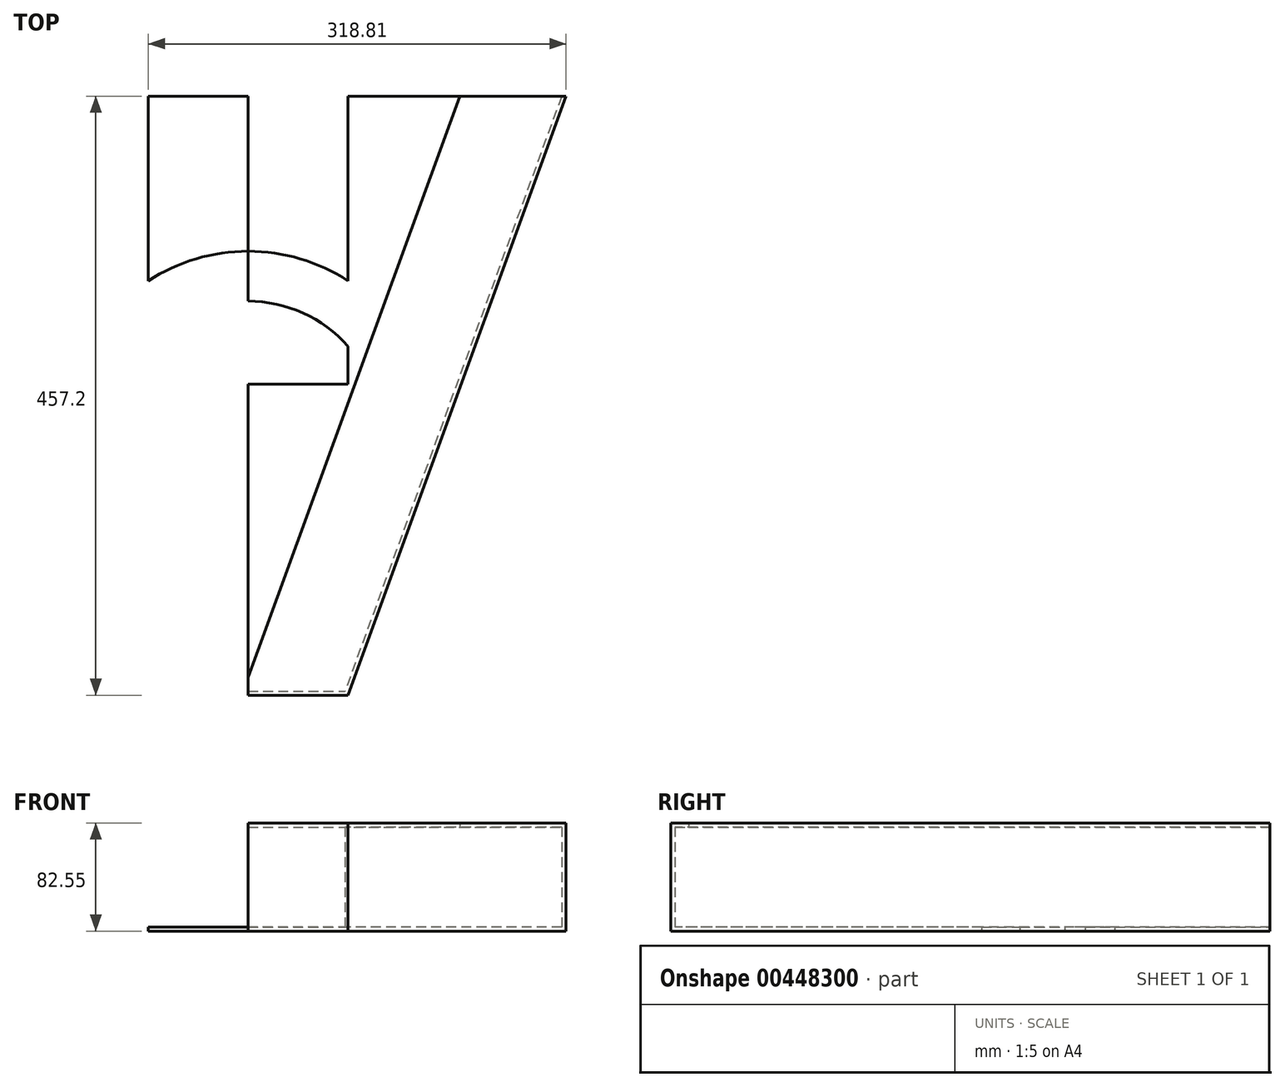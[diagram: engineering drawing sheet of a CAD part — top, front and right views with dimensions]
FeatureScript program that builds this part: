
annotation { "Feature Type Name" : "Feature", "Feature Type Description" : "" }
export const myFeature = defineFeature(function(context is Context, id is Id, definition is map)
    precondition{}
    {
        {
            var Q0;
            Q0=qCreatedBy(makeId("Top.planeOp"),FACE);
            var sketch = newSketch(context, id + "F0", { "sketchPlane" : qUnion([Q0])});
            skCircle(sketch, "E0", {"center": v(0, 0) * mm, "radius": 152.4 * mm});
            skLineSegment(sketch, "E1", {"start": v(-242.6, 220.97) * mm, "end": v(-76.2, -236.23) * mm});
            skLineSegment(sketch, "E2", {"start": v(-76.2, -236.23) * mm, "end": v(0, -236.23) * mm});
            skLineSegment(sketch, "E3", {"start": v(-242.6, 220.97) * mm, "end": v(0, 220.97) * mm});
            skLineSegment(sketch, "E4.MirrorCS", {"start": v(76.2, -236.23) * mm, "end": v(0, -236.23) * mm});
            skLineSegment(sketch, "E5.MirrorCS", {"start": v(242.6, 220.97) * mm, "end": v(0, 220.97) * mm});
            skLineSegment(sketch, "E6.MirrorCS", {"start": v(242.6, 220.97) * mm, "end": v(76.2, -236.23) * mm});
            skLineSegment(sketch, "E7", {"start": v(-76.2, -236.23) * mm, "end": v(-76.2, 220.97) * mm});
            skLineSegment(sketch, "E8.MirrorCS", {"start": v(76.2, -236.23) * mm, "end": v(76.2, 220.97) * mm});
            skLineSegment(sketch, "E9", {"start": v(-101.6, -166.44) * mm, "end": v(101.6, -166.44) * mm});
            skLineSegment(sketch, "E10", {"start": v(-242.6, 220.97) * mm, "end": v(-76.2, 145.12) * mm});
            skLineSegment(sketch, "E11.MirrorCS", {"start": v(242.6, 220.97) * mm, "end": v(76.2, 145.12) * mm});
            skLineSegment(sketch, "E12", {"start": v(-76.2, 145.12) * mm, "end": v(76.2, 145.12) * mm});
            skCircle(sketch, "E13", {"center": v(0, -37.13) * mm, "radius": 139.7 * mm});
            skLineSegment(sketch, "E14", {"start": v(-134.4, 0.97) * mm, "end": v(134.4, 0.97) * mm});
            skCircle(sketch, "E15", {"center": v(0, -37.13) * mm, "radius": 101.6 * mm});
            skLineSegment(sketch, "E16", {"start": v(0, 220.97) * mm, "end": v(0, -236.23) * mm});
            skSolve(sketch);
        }
        {
            var Q0;
            {var subQ0=sQuery(id+"F0.wireOp",EDGE,"E12");var subQ3=sQuery(id+"F0.wireOp",EDGE,"E0");var subQ4=makeQuery(id+"F0.imprint","INTERSECT",VERTEX,{"disambiguationData":[OD(0.0)],"derivedFrom":[subQ3,subQ0]});Q0=makeQuery(id+"F0.imprint","IMPRINT",FACE,{"disambiguationData":[TD([[makeQuery(id+"F0.imprint","IMPRINT",EDGE,{"disambiguationData":[TD([[subQ4,-1.0]])],"derivedFrom":subQ3}),-1.0]])]});}
            var Q1;
            {var subQ0=sQuery(id+"F0.wireOp",EDGE,"E12");var subQ1=sQuery(id+"F0.wireOp",EDGE,"E0");var subQ2=makeQuery(id+"F0.imprint","INTERSECT",VERTEX,{"disambiguationData":[OD(0.0)],"derivedFrom":[subQ1,subQ0]});Q1=makeQuery(id+"F0.imprint","IMPRINT",FACE,{"disambiguationData":[TD([[makeQuery(id+"F0.imprint","IMPRINT",EDGE,{"disambiguationData":[TD([[subQ2,-1.0]])],"derivedFrom":subQ1}),1.0]])]});}
            var Q2;
            {var subQ5=sQuery(id+"F0.wireOp",EDGE,"E12");var subQ6=sQuery(id+"F0.wireOp",EDGE,"E0");var subQ7=makeQuery(id+"F0.imprint","INTERSECT",VERTEX,{"disambiguationData":[OD(0.0)],"derivedFrom":[subQ6,subQ5]});Q2=makeQuery(id+"F0.imprint","IMPRINT",FACE,{"disambiguationData":[TD([[makeQuery(id+"F0.imprint","IMPRINT",EDGE,{"disambiguationData":[TD([[subQ7,1.0]])],"derivedFrom":subQ6}),1.0]])]});}
            var Q3;
            {var subQ0=sQuery(id+"F0.wireOp",EDGE,"E15");var subQ1=sQuery(id+"F0.wireOp",EDGE,"E8.MirrorCS");var subQ2=makeQuery(id+"F0.imprint","INTERSECT",VERTEX,{"disambiguationData":[OD(1.0)],"derivedFrom":[subQ1,subQ0]});Q3=makeQuery(id+"F0.imprint","IMPRINT",FACE,{"disambiguationData":[TD([[makeQuery(id+"F0.imprint","IMPRINT",EDGE,{"disambiguationData":[TD([[subQ2,-1.0]])],"derivedFrom":subQ1}),1.0]])]});}
            var Q4;
            {var subQ0=sQuery(id+"F0.wireOp",EDGE,"E15");var subQ1=sQuery(id+"F0.wireOp",EDGE,"E8.MirrorCS");var subQ2=makeQuery(id+"F0.imprint","INTERSECT",VERTEX,{"disambiguationData":[OD(1.0)],"derivedFrom":[subQ1,subQ0]});Q4=makeQuery(id+"F0.imprint","IMPRINT",FACE,{"disambiguationData":[TD([[makeQuery(id+"F0.imprint","IMPRINT",EDGE,{"disambiguationData":[TD([[subQ2,-1.0]])],"derivedFrom":subQ1}),-1.0]])]});}
            var Q5;
            {var subQ0=sQuery(id+"F0.wireOp",EDGE,"E14");var subQ1=sQuery(id+"F0.wireOp",EDGE,"E8.MirrorCS");var subQ2=makeQuery(id+"F0.imprint","INTERSECT",VERTEX,{"derivedFrom":[subQ1,subQ0]});Q5=makeQuery(id+"F0.imprint","IMPRINT",FACE,{"disambiguationData":[TD([[makeQuery(id+"F0.imprint","IMPRINT",EDGE,{"disambiguationData":[TD([[subQ2,-1.0]])],"derivedFrom":subQ1}),-1.0]])]});}
            var Q6;
            {var subQ0=sQuery(id+"F0.wireOp",EDGE,"E15");var subQ1=sQuery(id+"F0.wireOp",EDGE,"E8.MirrorCS");var subQ2=makeQuery(id+"F0.imprint","INTERSECT",VERTEX,{"disambiguationData":[OD(0.0)],"derivedFrom":[subQ1,subQ0]});Q6=makeQuery(id+"F0.imprint","IMPRINT",FACE,{"disambiguationData":[TD([[makeQuery(id+"F0.imprint","IMPRINT",EDGE,{"disambiguationData":[TD([[subQ2,-1.0]])],"derivedFrom":subQ1}),-1.0]])]});}
            var Q7;
            {var subQ0=sQuery(id+"F0.wireOp",EDGE,"E16");var subQ1=sQuery(id+"F0.wireOp",EDGE,"E0");var subQ2=makeQuery(id+"F0.imprint","INTERSECT",VERTEX,{"disambiguationData":[OD(1.0)],"derivedFrom":[subQ1,subQ0]});Q7=makeQuery(id+"F0.imprint","IMPRINT",FACE,{"disambiguationData":[TD([[makeQuery(id+"F0.imprint","IMPRINT",EDGE,{"disambiguationData":[TD([[subQ2,-1.0]])],"derivedFrom":subQ1}),1.0]])]});}
            var Q8;
            {var subQ0=sQuery(id+"F0.wireOp",EDGE,"E15");var subQ1=sQuery(id+"F0.wireOp",EDGE,"E8.MirrorCS");var subQ2=makeQuery(id+"F0.imprint","INTERSECT",VERTEX,{"disambiguationData":[OD(0.0)],"derivedFrom":[subQ1,subQ0]});Q8=makeQuery(id+"F0.imprint","IMPRINT",FACE,{"disambiguationData":[TD([[makeQuery(id+"F0.imprint","IMPRINT",EDGE,{"disambiguationData":[TD([[subQ2,-1.0]])],"derivedFrom":subQ1}),1.0]])]});}
            var Q9;
            {var subQ0=sQuery(id+"F0.wireOp",EDGE,"E16");var subQ6=sQuery(id+"F0.wireOp",EDGE,"E0");var subQ9=makeQuery(id+"F0.imprint","INTERSECT",VERTEX,{"disambiguationData":[OD(1.0)],"derivedFrom":[subQ6,subQ0]});Q9=makeQuery(id+"F0.imprint","IMPRINT",FACE,{"disambiguationData":[TD([[makeQuery(id+"F0.imprint","IMPRINT",EDGE,{"disambiguationData":[TD([[subQ9,-1.0]])],"derivedFrom":subQ6}),-1.0]])]});}
            var Q10;
            {var subQ7=sQuery(id+"F0.wireOp",EDGE,"E4.MirrorCS");Q10=makeQuery(id+"F0.imprint","IMPRINT",FACE,{"disambiguationData":[TD([[makeQuery(id+"F0.imprint","IMPRINT",EDGE,{"derivedFrom":subQ7}),-1.0]])]});}
            var Q11;
            {var subQ1=sQuery(id+"F0.wireOp",EDGE,"E6.MirrorCS");var subQ3=sQuery(id+"F0.wireOp",EDGE,"E9");var subQ4=makeQuery(id+"F0.imprint","INTERSECT",VERTEX,{"derivedFrom":[subQ1,subQ3]});Q11=makeQuery(id+"F0.imprint","IMPRINT",FACE,{"disambiguationData":[TD([[makeQuery(id+"F0.imprint","IMPRINT",EDGE,{"disambiguationData":[TD([[subQ4,1.0]])],"derivedFrom":subQ3}),-1.0]])]});}
            var Q12;
            {var subQ0=sQuery(id+"F0.wireOp",EDGE,"E9");var subQ1=sQuery(id+"F0.wireOp",EDGE,"E8.MirrorCS");var subQ2=makeQuery(id+"F0.imprint","INTERSECT",VERTEX,{"derivedFrom":[subQ1,subQ0]});Q12=makeQuery(id+"F0.imprint","IMPRINT",FACE,{"disambiguationData":[TD([[makeQuery(id+"F0.imprint","IMPRINT",EDGE,{"disambiguationData":[TD([[subQ2,-1.0]])],"derivedFrom":subQ1}),1.0]])]});}
            var Q13;
            {var subQ0=sQuery(id+"F0.wireOp",EDGE,"E16");var subQ1=sQuery(id+"F0.wireOp",EDGE,"E9");var subQ2=makeQuery(id+"F0.imprint","INTERSECT",VERTEX,{"derivedFrom":[subQ1,subQ0]});Q13=makeQuery(id+"F0.imprint","IMPRINT",FACE,{"disambiguationData":[TD([[makeQuery(id+"F0.imprint","IMPRINT",EDGE,{"disambiguationData":[TD([[subQ2,-1.0]])],"derivedFrom":subQ1}),-1.0]])]});}
            var Q14;
            {var subQ0=sQuery(id+"F0.wireOp",EDGE,"E9");var subQ1=sQuery(id+"F0.wireOp",EDGE,"E6.MirrorCS");var subQ2=makeQuery(id+"F0.imprint","INTERSECT",VERTEX,{"derivedFrom":[subQ1,subQ0]});Q14=makeQuery(id+"F0.imprint","IMPRINT",FACE,{"disambiguationData":[TD([[makeQuery(id+"F0.imprint","IMPRINT",EDGE,{"disambiguationData":[TD([[subQ2,1.0]])],"derivedFrom":subQ1}),-1.0]])]});}
            var Q15;
            {var subQ0=sQuery(id+"F0.wireOp",EDGE,"E8.MirrorCS");var subQ1=sQuery(id+"F0.wireOp",EDGE,"E0");var subQ2=makeQuery(id+"F0.imprint","INTERSECT",VERTEX,{"disambiguationData":[OD(1.0)],"derivedFrom":[subQ1,subQ0]});Q15=makeQuery(id+"F0.imprint","IMPRINT",FACE,{"disambiguationData":[TD([[makeQuery(id+"F0.imprint","IMPRINT",EDGE,{"disambiguationData":[TD([[subQ2,-1.0]])],"derivedFrom":subQ1}),-1.0]])]});}
            var Q16;
            {var subQ5=sQuery(id+"F0.wireOp",EDGE,"E0");var subQ7=sQuery(id+"F0.wireOp",EDGE,"E8.MirrorCS");var subQ8=makeQuery(id+"F0.imprint","INTERSECT",VERTEX,{"disambiguationData":[OD(1.0)],"derivedFrom":[subQ5,subQ7]});Q16=makeQuery(id+"F0.imprint","IMPRINT",FACE,{"disambiguationData":[TD([[makeQuery(id+"F0.imprint","IMPRINT",EDGE,{"disambiguationData":[TD([[subQ8,-1.0]])],"derivedFrom":subQ5}),1.0]])]});}
            var Q17;
            {var subQ4=sQuery(id+"F0.wireOp",EDGE,"E0");var subQ6=makeQuery(id+"F0.imprint","INTERSECT",VERTEX,{"derivedFrom":[subQ4,sQuery(id+"F0.wireOp",EDGE,"E6.MirrorCS")]});Q17=makeQuery(id+"F0.imprint","IMPRINT",FACE,{"disambiguationData":[TD([[makeQuery(id+"F0.imprint","IMPRINT",EDGE,{"disambiguationData":[TD([[subQ6,1.0]])],"derivedFrom":subQ4}),1.0]])]});}
            var Q18;
            {var subQ5=sQuery(id+"F0.wireOp",EDGE,"E11.MirrorCS");Q18=makeQuery(id+"F0.imprint","IMPRINT",FACE,{"disambiguationData":[TD([[makeQuery(id+"F0.imprint","IMPRINT",EDGE,{"derivedFrom":subQ5}),1.0]])]});}
            var Q19;
            {var subQ0=sQuery(id+"F0.wireOp",EDGE,"E12");var subQ1=sQuery(id+"F0.wireOp",EDGE,"E0");var subQ2=makeQuery(id+"F0.imprint","INTERSECT",VERTEX,{"disambiguationData":[OD(0.0)],"derivedFrom":[subQ1,subQ0]});Q19=makeQuery(id+"F0.imprint","IMPRINT",FACE,{"disambiguationData":[TD([[makeQuery(id+"F0.imprint","IMPRINT",EDGE,{"disambiguationData":[TD([[subQ2,1.0]])],"derivedFrom":subQ1}),-1.0]])]});}
            var Q20;
            {var subQ0=sQuery(id+"F0.wireOp",EDGE,"E11.MirrorCS");Q20=makeQuery(id+"F0.imprint","IMPRINT",FACE,{"disambiguationData":[TD([[makeQuery(id+"F0.imprint","IMPRINT",EDGE,{"derivedFrom":subQ0}),-1.0]])]});}
            var Q21;
            {var subQ0=sQuery(id+"F0.wireOp",EDGE,"E6.MirrorCS");var subQ1=sQuery(id+"F0.wireOp",EDGE,"E0");var subQ2=makeQuery(id+"F0.imprint","INTERSECT",VERTEX,{"derivedFrom":[subQ1,subQ0]});Q21=makeQuery(id+"F0.imprint","IMPRINT",FACE,{"disambiguationData":[TD([[makeQuery(id+"F0.imprint","IMPRINT",EDGE,{"disambiguationData":[TD([[subQ2,1.0]])],"derivedFrom":subQ1}),-1.0]])]});}
            extrude(context, id + "F1", {"entities" : qUnion([Q0, Q1, Q2, Q3, Q4, Q5, Q6, Q7, Q8, Q9, Q10, Q11, Q12, Q13, Q14, Q15, Q16, Q17, Q18, Q19, Q20, Q21]), "depth" : 3.17 * mm});
        }
        {
            var Q0;
            Q0=makeQuery(id+"F1.opExtrude","CAP_FACE",FACE,{"disambiguationData":[OSD([sQuery(id+"F0.wireOp",EDGE,"E0"),sQuery(id+"F0.wireOp",EDGE,"E4.MirrorCS"),sQuery(id+"F0.wireOp",EDGE,"E5.MirrorCS"),sQuery(id+"F0.wireOp",EDGE,"E6.MirrorCS"),sQuery(id+"F0.wireOp",EDGE,"E8.MirrorCS"),sQuery(id+"F0.wireOp",EDGE,"E13"),sQuery(id+"F0.wireOp",EDGE,"E14"),sQuery(id+"F0.wireOp",EDGE,"E15"),sQuery(id+"F0.wireOp",EDGE,"E16")])],"isStart":false});
            var sketch = newSketch(context, id + "F2", { "sketchPlane" : qUnion([Q0])});
            skLineSegment(sketch, "E17", {"start": v(239.23, 220.97) * mm, "end": v(72.82, -236.23) * mm});
            skLineSegment(sketch, "E18", {"start": v(0, -233.06) * mm, "end": v(77.36, -233.06) * mm});
            skSolve(sketch);
        }
        {
            var Q0;
            {var subQ0=sQuery(id+"F2.wireOp",EDGE,"E17");var subQ1=makeQuery(id+"F1.opExtrude","CAP_EDGE",EDGE,{"disambiguationData":[OSD([sQuery(id+"F0.wireOp",EDGE,"E5.MirrorCS")])],"isStart":false});var subQ2=makeQuery(id+"F2.imprint","INTERSECT",VERTEX,{"derivedFrom":[subQ1,subQ0]});Q0=makeQuery(id+"F2.imprint","IMPRINT",FACE,{"disambiguationData":[TD([[makeQuery(id+"F2.imprint","IMPRINT",EDGE,{"disambiguationData":[TD([[subQ2,-1.0]])],"derivedFrom":subQ0}),1.0]])]});}
            var Q1;
            {var subQ0=sQuery(id+"F2.wireOp",EDGE,"E17");var subQ1=makeQuery(id+"F1.opExtrude","CAP_EDGE",EDGE,{"disambiguationData":[OSD([sQuery(id+"F0.wireOp",EDGE,"E4.MirrorCS")])],"isStart":false});var subQ2=makeQuery(id+"F2.imprint","INTERSECT",VERTEX,{"derivedFrom":[subQ1,subQ0]});Q1=makeQuery(id+"F2.imprint","IMPRINT",FACE,{"disambiguationData":[TD([[makeQuery(id+"F2.imprint","IMPRINT",EDGE,{"disambiguationData":[TD([[subQ2,1.0]])],"derivedFrom":subQ0}),1.0]])]});}
            var Q2;
            {var subQ0=sQuery(id+"F2.wireOp",EDGE,"E17");var subQ1=sQuery(id+"F0.wireOp",EDGE,"E4.MirrorCS");var subQ2=makeQuery(id+"F1.opExtrude","CAP_EDGE",EDGE,{"disambiguationData":[OSD([subQ1])],"isStart":false});var subQ3=makeQuery(id+"F2.imprint","INTERSECT",VERTEX,{"derivedFrom":[subQ2,subQ0]});Q2=makeQuery(id+"F2.imprint","IMPRINT",FACE,{"disambiguationData":[TD([[makeQuery(id+"F2.imprint","IMPRINT",EDGE,{"disambiguationData":[TD([[subQ3,1.0]])],"derivedFrom":subQ0}),-1.0]])]});}
            extrude(context, id + "F3", {"entities" : qUnion([Q0, Q1, Q2]), "operationType" : NewBodyOperationType.ADD, "depth" : 76.2 * mm});
        }
        {
            var Q0;
            Q0=makeQuery(id+"F3.opExtrude","CAP_FACE",FACE,{"disambiguationData":[OSD([sQuery(id+"F0.wireOp",EDGE,"E4.MirrorCS"),sQuery(id+"F0.wireOp",EDGE,"E5.MirrorCS"),sQuery(id+"F0.wireOp",EDGE,"E6.MirrorCS"),sQuery(id+"F0.wireOp",EDGE,"E16"),sQuery(id+"F2.wireOp",EDGE,"E17"),sQuery(id+"F2.wireOp",EDGE,"E18")])],"isStart":false});
            var sketch = newSketch(context, id + "F4", { "sketchPlane" : qUnion([Q0])});
            skLineSegment(sketch, "E19", {"start": v(161.52, 220.97) * mm, "end": v(242.6, 220.97) * mm});
            skLineSegment(sketch, "E20", {"start": v(242.6, 220.97) * mm, "end": v(76.2, -236.23) * mm});
            skLineSegment(sketch, "E21", {"start": v(76.2, -236.23) * mm, "end": v(0, -236.23) * mm});
            skLineSegment(sketch, "E22", {"start": v(0, -236.23) * mm, "end": v(0, -222.8) * mm});
            skLineSegment(sketch, "E23", {"start": v(0, -222.8) * mm, "end": v(161.52, 220.97) * mm});
            skSolve(sketch);
        }
        {
            var Q0;
            {var subQ0=makeQuery(id+"F3.opExtrude","CAP_EDGE",EDGE,{"disambiguationData":[OSD([sQuery(id+"F2.wireOp",EDGE,"E17")])],"isStart":false});Q0=makeQuery(id+"F4.imprint","IMPRINT",FACE,{"disambiguationData":[TD([[makeQuery(id+"F4.imprint","IMPRINT",EDGE,{"derivedFrom":subQ0}),-1.0]])]});}
            var Q1;
            {var subQ3=sQuery(id+"F4.wireOp",EDGE,"E20");Q1=makeQuery(id+"F4.imprint","IMPRINT",FACE,{"disambiguationData":[TD([[makeQuery(id+"F4.imprint","IMPRINT",EDGE,{"derivedFrom":subQ3}),-1.0]])]});}
            extrude(context, id + "F5", {"entities" : qUnion([Q0, Q1]), "operationType" : NewBodyOperationType.ADD, "depth" : 3.17 * mm});
        }
    });
